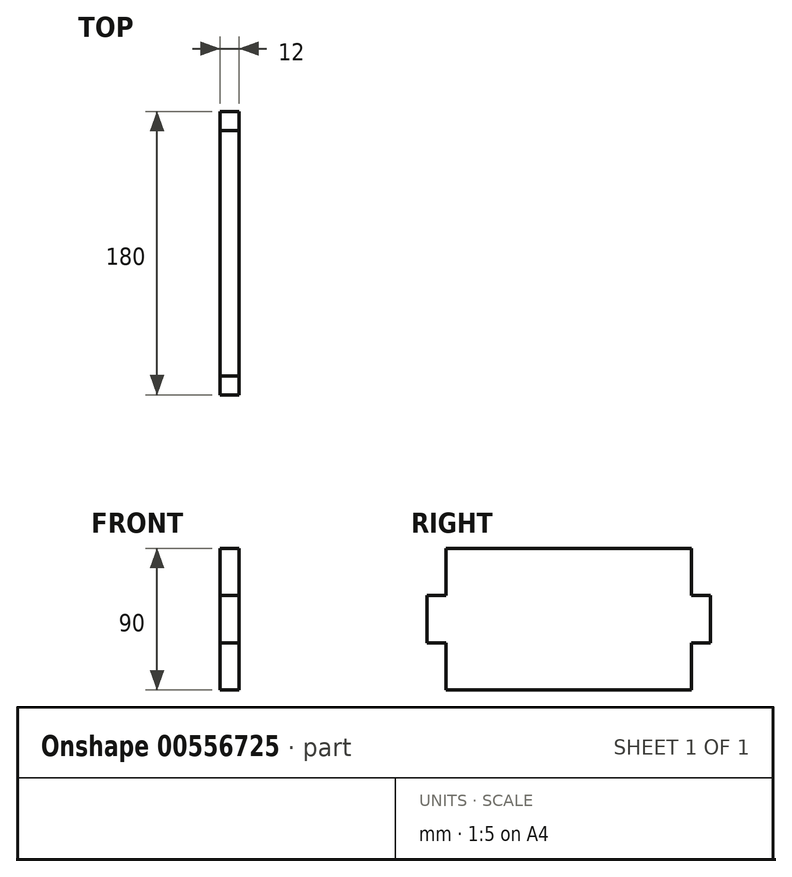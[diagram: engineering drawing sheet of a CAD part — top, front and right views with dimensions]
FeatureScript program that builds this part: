
annotation { "Feature Type Name" : "Feature", "Feature Type Description" : "" }
export const myFeature = defineFeature(function(context is Context, id is Id, definition is map)
    precondition{}
    {
        {
            var Q0;
            Q0=qCreatedBy(makeId("Right.planeOp"),FACE);
            var sketch = newSketch(context, id + "F0", { "sketchPlane" : qUnion([Q0])});
            skLineSegment(sketch, "E0", {"start": v(0, 0) * mm, "end": v(12, 0) * mm});
            skLineSegment(sketch, "E1", {"start": v(12, 0) * mm, "end": v(12, 30) * mm});
            skLineSegment(sketch, "E2", {"start": v(12, 30) * mm, "end": v(0, 30) * mm});
            skLineSegment(sketch, "E3", {"start": v(0, 30) * mm, "end": v(0, 60) * mm});
            skLineSegment(sketch, "E4", {"start": v(0, 60) * mm, "end": v(12, 60) * mm});
            skLineSegment(sketch, "E5", {"start": v(12, 60) * mm, "end": v(12, 90) * mm});
            skLineSegment(sketch, "E6", {"start": v(12, 90) * mm, "end": v(90, 90) * mm});
            skLineSegment(sketch, "E7", {"start": v(90, 90) * mm, "end": v(90, 0) * mm, "construction": true});
            skLineSegment(sketch, "E8", {"start": v(90, 0) * mm, "end": v(12, 0) * mm});
            skLineSegment(sketch, "E9.MirrorCS", {"start": v(180, 30) * mm, "end": v(180, 60) * mm});
            skLineSegment(sketch, "E10.MirrorCS", {"start": v(180, 60) * mm, "end": v(168, 60) * mm});
            skLineSegment(sketch, "E11.MirrorCS", {"start": v(168, 30) * mm, "end": v(180, 30) * mm});
            skLineSegment(sketch, "E12.MirrorCS", {"start": v(168, 0) * mm, "end": v(168, 30) * mm});
            skLineSegment(sketch, "E13.MirrorCS", {"start": v(90, 0) * mm, "end": v(168, 0) * mm});
            skLineSegment(sketch, "E14.MirrorCS", {"start": v(168, 90) * mm, "end": v(90, 90) * mm});
            skLineSegment(sketch, "E15.MirrorCS", {"start": v(180, 0) * mm, "end": v(168, 0) * mm});
            skLineSegment(sketch, "E16.MirrorCS", {"start": v(168, 60) * mm, "end": v(168, 90) * mm});
            skSolve(sketch);
        }
        {
            var Q0;
            Q0 = qSketchRegion(id + "F0", true);
            extrude(context, id + "F1", {"entities" : qUnion([Q0]), "endBound" : BoundingType.SYMMETRIC, "depth" : 12 * mm, "offsetDistance" : 25 * mm});
        }
    });
